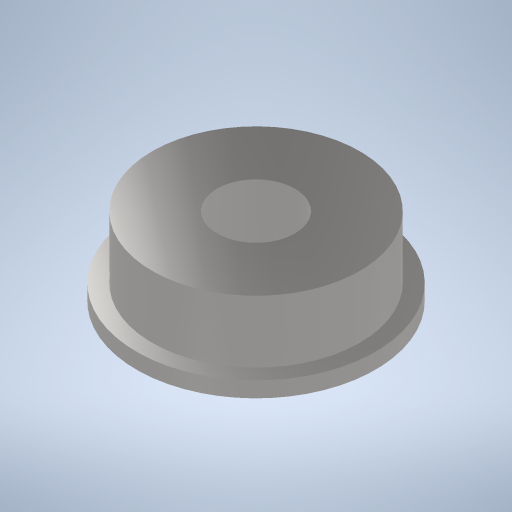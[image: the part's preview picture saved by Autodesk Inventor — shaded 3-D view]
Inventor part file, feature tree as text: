
AUTODESK INVENTOR PART (.ipt)
format: ipt  version: 2023 (Build 270158000, 158)  size: 240,128 bytes
history: native  units: mm
features: extrude x2, sketch x1
ambient origin geometry x8: Origin, YZ Plane, XZ Plane, XY Plane, X Axis, Y Axis, Z Axis, Center Point
bodies: Volumenkörper1 (feature_tree)
feature tree (3):
  sketch  "Skizze1"  dims[d0=9.2mm d1=8.0mm d2=3.0mm d3=0.6mm d4=0.0mm d5=3.0mm d6=0.0mm d7=0.5mm d8=0.872665mm]
  extrude  "Extrusion1"  Depth=3.0mm
  extrude  "Extrusion2"  Depth=3.0mm
